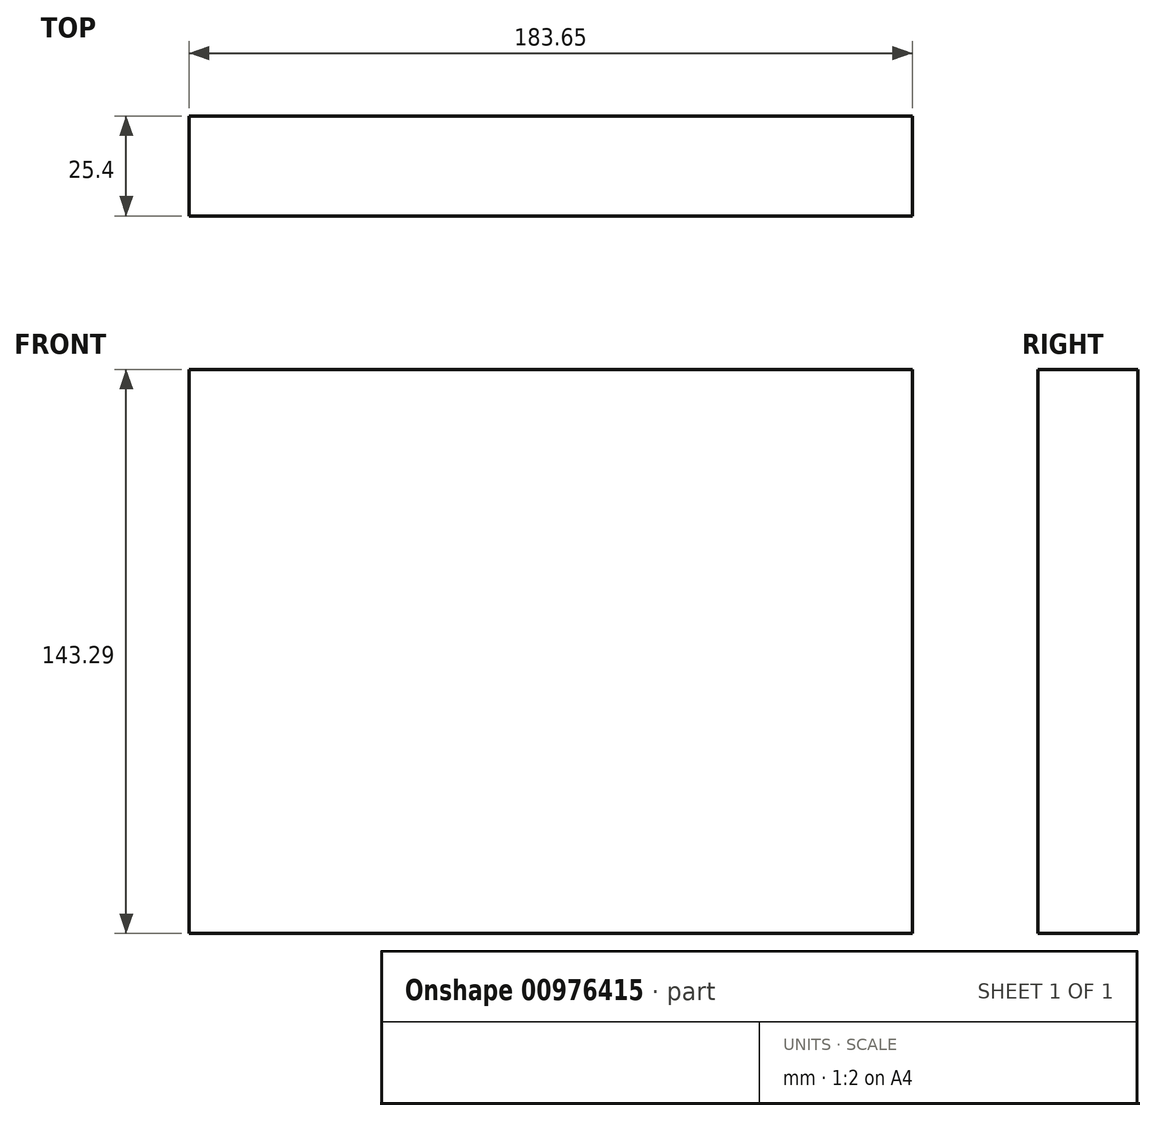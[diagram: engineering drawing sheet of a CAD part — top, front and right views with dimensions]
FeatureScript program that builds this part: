
annotation { "Feature Type Name" : "Feature", "Feature Type Description" : "" }
export const myFeature = defineFeature(function(context is Context, id is Id, definition is map)
    precondition{}
    {
        {
            var Q0;
            Q0=qCreatedBy(makeId("Front.planeOp"),FACE);
            var sketch = newSketch(context, id + "F0", { "sketchPlane" : qUnion([Q0])});
            skLineSegment(sketch, "E0.bottom", {"start": v(-90.09, 74.14) * mm, "end": v(93.56, 74.14) * mm});
            skLineSegment(sketch, "E0.top", {"start": v(-90.09, -69.15) * mm, "end": v(93.56, -69.15) * mm});
            skLineSegment(sketch, "E0.left", {"start": v(-90.09, 74.14) * mm, "end": v(-90.09, -69.15) * mm});
            skLineSegment(sketch, "E0.right", {"start": v(93.56, 74.14) * mm, "end": v(93.56, -69.15) * mm});
            skSolve(sketch);
        }
        {
            var Q0;
            Q0=makeQuery(id+"F0.imprint","IMPRINT",FACE,{"disambiguationData":[TD([[makeQuery(id+"F0.imprint","IMPRINT",EDGE,{"derivedFrom":sQuery(id+"F0.wireOp",EDGE,"E0.bottom")}),-1.0]])]});
            extrude(context, id + "F1", {"entities" : qUnion([Q0]), "depth" : 25.4 * mm, "offsetDistance" : 25.4 * mm});
        }
    });
